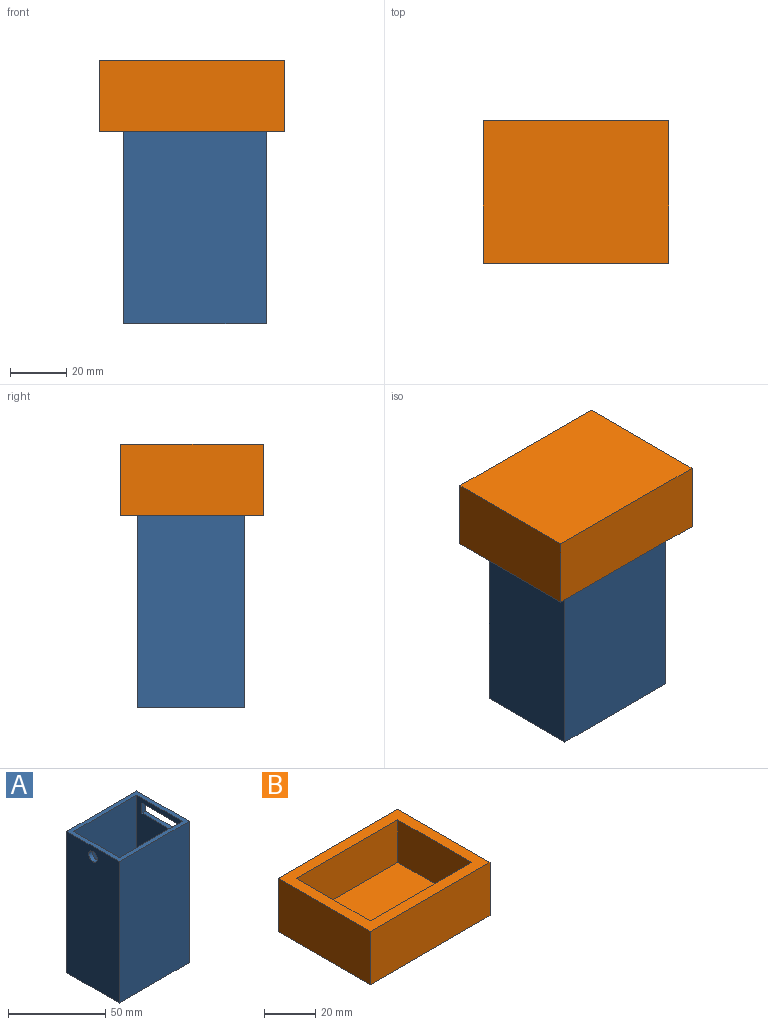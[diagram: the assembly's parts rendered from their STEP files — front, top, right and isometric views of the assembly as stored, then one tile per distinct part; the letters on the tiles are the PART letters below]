
ASSEMBLY  parts=2 mates=1
PART A: 16 faces, bbox 50.8x38.1x88.9 mm
  f0: plane 88.9x38.1mm, normal (1,0,0), area 3225.8mm2, adj f2,f4,f5,f6,f12,f13,f14,f15
  f1: plane 86.36x33.02mm, normal (-1,0,0), area 2690.3mm2, adj f2,f8,f9,f10,f12,f13,f14,f15
  f2: plane 50.8x38.1mm, normal (0,0,1), area 425.8mm2, adj f0,f1,f3,f4,f5,f7,f8,f9
  f3: plane 88.9x38.1mm, normal (-1,0,0), area 3355.4mm2, adj f2,f4,f5,f6,f11
  f4: plane 88.9x50.8mm, normal (0,-1,0), area 4516.1mm2, adj f0,f2,f3,f6
  f5: plane 88.9x50.8mm, normal (0,1,0), area 4516.1mm2, adj f0,f2,f3,f6
  f6: plane 50.8x38.1mm, normal (0,0,-1), area 1935.5mm2, adj f0,f3,f4,f5
  f7: plane 86.36x33.02mm, normal (1,0,0), area 2819.9mm2, adj f2,f8,f9,f10,f11
  f8: plane 86.36x45.72mm, normal (0,1,0), area 3948.4mm2, adj f1,f2,f7,f10
  f9: plane 86.36x45.72mm, normal (0,-1,0), area 3948.4mm2, adj f1,f2,f7,f10
  f10: plane 45.72x33.02mm, normal (0,0,1), area 1509.7mm2, adj f1,f7,f8,f9
  f11: cylinder r=3.17mm len=6.35mm, axis (-1,0,0), area 50.7mm2, adj f3,f7
  f12: plane 25.4x2.54mm, normal (0,0,-1), area 64.5mm2, adj f0,f1,f13,f15
  f13: plane 6.35x2.54mm, normal (0,1,0), area 16.1mm2, adj f0,f1,f12,f14
  f14: plane 25.4x2.54mm, normal (0,0,1), area 64.5mm2, adj f0,f1,f13,f15
  f15: plane 6.35x2.54mm, normal (0,-1,0), area 16.1mm2, adj f0,f1,f12,f14
PART B: 11 faces, bbox 66x50.8x25.4 mm
  f0: plane 66.04x50.8mm, normal (0,0,1), area 1083.9mm2, adj f1,f2,f3,f4,f6,f7,f8,f9
  f1: plane 50.8x25.4mm, normal (-1,0,0), area 1290.3mm2, adj f0,f2,f4,f5
  f2: plane 66.04x25.4mm, normal (0,-1,0), area 1677.4mm2, adj f0,f1,f3,f5
  f3: plane 50.8x25.4mm, normal (1,0,0), area 1290.3mm2, adj f0,f2,f4,f5
  f4: plane 66.04x25.4mm, normal (0,1,0), area 1677.4mm2, adj f0,f1,f3,f5
  f5: plane 66.04x50.8mm, normal (0,0,-1), area 3354.8mm2, adj f1,f2,f3,f4
  f6: plane 40.64x20.32mm, normal (1,0,0), area 825.8mm2, adj f0,f7,f9,f10
  f7: plane 55.88x20.32mm, normal (0,1,0), area 1135.5mm2, adj f0,f6,f8,f10
  f8: plane 40.64x20.32mm, normal (-1,0,0), area 825.8mm2, adj f0,f7,f9,f10
  f9: plane 55.88x20.32mm, normal (0,-1,0), area 1135.5mm2, adj f0,f6,f8,f10
  f10: plane 55.88x40.64mm, normal (0,0,1), area 2271mm2, adj f6,f7,f8,f9
PLACE A rot(axis=(-1,0,0),0deg) t=(-3.9,27.1,5.93)mm
PLACE B rot(axis=(1,0,0),180deg) t=(-12.54,71.3,99.91)mm
MATE planar A.f2 <-> B.f10  axis (0,0,1) through (-1.36,29.64,94.83)mm
